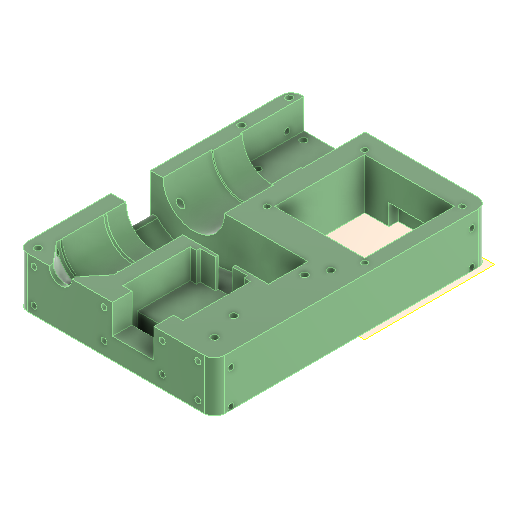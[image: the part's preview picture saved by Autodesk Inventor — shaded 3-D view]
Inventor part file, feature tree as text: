
AUTODESK INVENTOR PART (.ipt)
format: ipt  version: 2024.1 (Build 281209000, 209)  size: 511,488 bytes
history: native  units: mm
features: reference x21, sketch x11, other x9, projected_geometry x7, extrude x6, hole x4, plane x2, fillet x2, revolve x1
ambient origin geometry x8: Origin, YZ Plane, XZ Plane, XY Plane, X Axis, Y Axis, Z Axis, Center Point
bodies: Volumenkörper1 (feature_tree)
feature tree (63):
  plane  "Arbeitsebene1"
  plane  "Arbeitsebene2"
  extrude  "Extrusion1"  Depth=2.8mm
  revolve  "Umdrehung1"
  extrude  "Extrusion2"  Depth=2.8mm
  extrude  "Extrusion3"  Depth=95.0mm
  extrude  "Extrusion4"  Depth=50.0mm TaperAngle=0.0deg
  hole  "Bohrung1"  [1 undecoded]
  hole  "Bohrung2"  [1 undecoded]
  hole  "Bohrung4"  [1 undecoded]
  fillet  "Rundung1"  Radius=12.0mm
  extrude  "Extrusion6"  Depth=14.0mm
  extrude  "Extrusion7"  Depth=1.0mm TaperAngle=0.0deg
  fillet  "Rundung2"  Radius=0.3mm
  hole  "Bohrung6"  [1 undecoded]
  sketch  "Skizze1"  dims[d0=0.5mm d1=2.8mm]
  reference  "Referenz1"
  reference  "Referenz2"
  reference  "Referenz3"
  reference  "Referenz4"
  reference  "Referenz5"
  reference  "Referenz6"
  reference  "Referenz7"
  reference  "Referenz8"
  reference  "Referenz9"
  reference  "Referenz10"
  sketch  "Skizze2"  dims[d2=2.8mm d3=2.8mm]
  projected_geometry  "Projizierte Kontur1"
  reference  "Referenz11"
  reference  "Referenz12"
  sketch  "Skizze3"  dims[d4=2.8mm d5=95.0mm]
  reference  "Referenz13"
  reference  "Referenz14"
  reference  "Referenz15"
  reference  "Referenz16"
  sketch  "Skizze4"  dims[d6=132.0mm d7=50.0mm d8=0.0mm]
  reference  "Referenz17"
  reference  "Referenz18"
  sketch  "Skizze5"  dims[d9=0.25mm d10=360.0deg]
  projected_geometry  "Projizierte Kontur2"
  reference  "Referenz19"
  reference  "Referenz20"
  sketch  "Skizze6"  dims[d11=20.0mm d12=0.5mm]
  projected_geometry  "Projizierte Kontur3"
  sketch  "Skizze8"  dims[d13=0.5mm d14=14.1mm d15=0.0mm d16=12.0mm]
  projected_geometry  "Projizierte Kontur4"
  sketch  "Skizze10"  dims[d17=11.0mm d18=14.0mm]
  projected_geometry  "Projizierte Kontur5"
  sketch  "Skizze12"  dims[d19=18.0mm d20=0.0mm d21=1.0mm d22=0.0mm d23=0.3mm]
  projected_geometry  "Projizierte Kontur7"
  sketch  "Skizze13"  dims[d24=14.3mm d25=0.0mm d26=10.0mm]
  projected_geometry  "Projizierte Kontur8"
  sketch  "Skizze14"  dims[d27=3.3mm d28=6.0mm d29=6.5mm d30=8.0mm d31=90.0deg d32=8.0mm d33=20.594885mm d34=3.0mm d35=3.0mm d41=31.15mm d43=2.8mm d44=6.0mm d45=6.5mm d46=8.0mm d47=90.0deg d48=12.0mm d49=20.594885mm d58=2.8mm d59=6.0mm d60=4.0mm d61=2.0mm d62=90.0deg d63=12.0mm d64=20.594885mm d74=1.0mm d75=2.25mm d76=2.0mm d77=7.0mm d78=0.0mm d79=0.0mm d80=20.0mm d81=9.0mm d82=10.0mm d83=0.0mm d84=5.0mm d85=2.8mm d86=6.0mm d87=4.0mm d88=2.0mm d89=90.0deg d90=12.0mm d91=20.594885mm]
  reference  "Referenz25"
  other  "Assembly_Planktoscope_Uc2version_V1.iam"
  other  "00_NEMA17_Perestalticpump_Adapter:1"
  other  "00_NEMA_17:1"
  other  "00_HIKCamera_MV-CE060-10UMUC:1"
  other  "00_Microscope_Slide:2"
  other  "00_CCTV_Lens_Hikvision_50mm_2.8:1"
  other  "00_NEMA11:3"
  other  "60_Planktoscope_Wallboxmoutingplate:1"
  other  "Assembly_Planktoscope_Uc2version_V!.iam"
note: 4 required parameter values undecoded (feature->parameter linkage not recoverable at this tier; creation-order binding heuristic only, values carry confidence <= 0.55)
